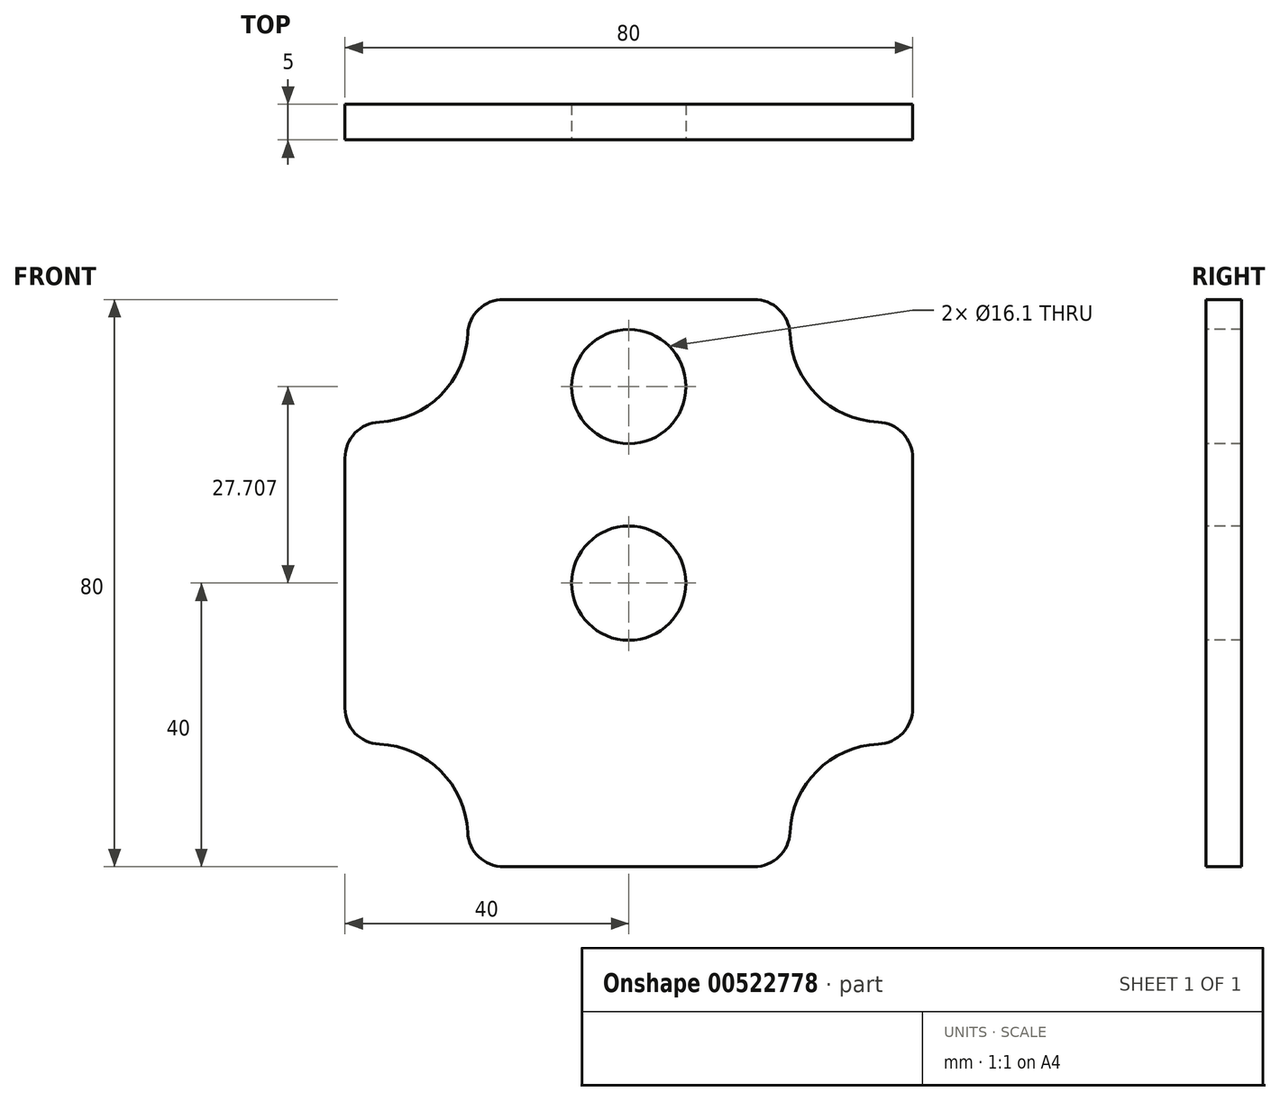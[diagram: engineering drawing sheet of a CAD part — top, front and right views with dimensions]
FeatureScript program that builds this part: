
annotation { "Feature Type Name" : "Feature", "Feature Type Description" : "" }
export const myFeature = defineFeature(function(context is Context, id is Id, definition is map)
    precondition{}
    {
        {
            var Q0;
            Q0=qCreatedBy(makeId("Front.planeOp"),FACE);
            var sketch = newSketch(context, id + "F0", { "sketchPlane" : qUnion([Q0])});
            skLineSegment(sketch, "E0", {"start": v(-40, 0) * mm, "end": v(-40, 23.43) * mm});
            skLineSegment(sketch, "E1", {"start": v(-40, 23.43) * mm, "end": v(-23.43, 40) * mm});
            skLineSegment(sketch, "E2", {"start": v(-23.43, 40) * mm, "end": v(0, 40) * mm});
            skLineSegment(sketch, "E3", {"start": v(-40, 0) * mm, "end": v(0, 0) * mm});
            skLineSegment(sketch, "E4", {"start": v(0, 0) * mm, "end": v(0, 40) * mm});
            skArc(sketch, "E5", {"start": v(-40, 23.43) * mm, "mid": v(-26.5, 26.5) * mm, "end": v(-23.43, 40) * mm});
            skSolve(sketch);
        }
        {
            var Q0;
            Q0=makeQuery(id+"F0.imprint","IMPRINT",FACE,{"disambiguationData":[TD([[makeQuery(id+"F0.imprint","IMPRINT",EDGE,{"derivedFrom":sQuery(id+"F0.wireOp",EDGE,"E0")}),-1.0]])]});
            extrude(context, id + "F1", {"entities" : qUnion([Q0]), "depth" : 5 * mm, "offsetDistance" : 25.4 * mm});
        }
        {
            var Q0;
            Q0=makeQuery(id+"F1.opExtrude","SWEPT_BODY",BODY,{"disambiguationData":[OSD([sQuery(id+"F0.wireOp",EDGE,"E0"),sQuery(id+"F0.wireOp",EDGE,"E1"),sQuery(id+"F0.wireOp",EDGE,"E2"),sQuery(id+"F0.wireOp",EDGE,"E3"),sQuery(id+"F0.wireOp",EDGE,"E4")])]});
            var Q1;
            Q1=makeQuery(id+"F1.opExtrude","SWEPT_FACE",FACE,{"disambiguationData":[OSD([sQuery(id+"F0.wireOp",EDGE,"E4")])]});
            mirror(context, id + "F2", {"operationType" : NewBodyOperationType.ADD, "entities" : qUnion([Q0]), "mirrorPlane" : qUnion([Q1])});
        }
        {
            var Q0;
            Q0=makeQuery(id+"F1.opExtrude","SWEPT_BODY",BODY,{"disambiguationData":[OSD([sQuery(id+"F0.wireOp",EDGE,"E0"),sQuery(id+"F0.wireOp",EDGE,"E1"),sQuery(id+"F0.wireOp",EDGE,"E2"),sQuery(id+"F0.wireOp",EDGE,"E3"),sQuery(id+"F0.wireOp",EDGE,"E4")])]});
            var Q1;
            {var subQ0=makeQuery(id+"F1.opExtrude","SWEPT_FACE",FACE,{"disambiguationData":[OSD([sQuery(id+"F0.wireOp",EDGE,"E3")])]});Q1=makeQuery(id+"F2.boolean.opBoolean","MERGE",FACE,{"derivedFrom":[subQ0,makeQuery(id+"F2.opPattern","COPY",FACE,{"derivedFrom":subQ0,"instanceName":"1"})]});}
            mirror(context, id + "F3", {"operationType" : NewBodyOperationType.ADD, "entities" : qUnion([Q0]), "mirrorPlane" : qUnion([Q1])});
        }
        {
            var Q0;
            {var subQ0=makeQuery(id+"F1.opExtrude","CAP_FACE",FACE,{"disambiguationData":[OSD([sQuery(id+"F0.wireOp",EDGE,"E0"),sQuery(id+"F0.wireOp",EDGE,"E1"),sQuery(id+"F0.wireOp",EDGE,"E2"),sQuery(id+"F0.wireOp",EDGE,"E3"),sQuery(id+"F0.wireOp",EDGE,"E4")])],"isStart":false});var subQ1=makeQuery(id+"F2.boolean.opBoolean","MERGE",FACE,{"derivedFrom":[subQ0,makeQuery(id+"F2.opPattern","COPY",FACE,{"derivedFrom":subQ0,"instanceName":"1"})]});Q0=makeQuery(id+"F3.boolean.opBoolean","MERGE",FACE,{"derivedFrom":[subQ1,makeQuery(id+"F3.opPattern","COPY",FACE,{"derivedFrom":subQ1,"instanceName":"1"})]});}
            var sketch = newSketch(context, id + "F4", { "sketchPlane" : qUnion([Q0])});
            skCircle(sketch, "E6", {"center": v(0, 0) * mm, "radius": 8.05 * mm});
            skCircle(sketch, "E7.0", {"center": v(0, 0) * mm, "radius": 14.4 * mm});
            skSolve(sketch);
        }
        {
            var Q0;
            Q0=makeQuery(id+"F4.imprint","IMPRINT",FACE,{"disambiguationData":[TD([[makeQuery(id+"F4.imprint","IMPRINT",EDGE,{"derivedFrom":sQuery(id+"F4.wireOp",EDGE,"E6")}),1.0]])]});
            extrude(context, id + "F5", {"entities" : qUnion([Q0]), "operationType" : NewBodyOperationType.REMOVE, "endBound" : BoundingType.THROUGH_ALL, "oppositeDirection" : true, "depth" : 25.4 * mm, "offsetDistance" : 25.4 * mm});
        }
        {
            var Q0;
            Q0=makeQuery(id+"F1.opExtrude","SWEPT_EDGE",EDGE,{"disambiguationData":[OSD([sQuery(id+"F0.wireOp",EDGE,"E0"),sQuery(id+"F0.wireOp",EDGE,"E1"),sQuery(id+"F0.wireOp",EDGE,"E5")])]});
            var Q1;
            Q1=makeQuery(id+"F1.opExtrude","SWEPT_EDGE",EDGE,{"disambiguationData":[OSD([sQuery(id+"F0.wireOp",EDGE,"E1"),sQuery(id+"F0.wireOp",EDGE,"E2"),sQuery(id+"F0.wireOp",EDGE,"E5")])]});
            var Q2;
            Q2=makeQuery(id+"F2.opPattern","COPY",EDGE,{"derivedFrom":makeQuery(id+"F1.opExtrude","SWEPT_EDGE",EDGE,{"disambiguationData":[OSD([sQuery(id+"F0.wireOp",EDGE,"E1"),sQuery(id+"F0.wireOp",EDGE,"E2"),sQuery(id+"F0.wireOp",EDGE,"E5")])]}),"instanceName":"1"});
            var Q3;
            Q3=makeQuery(id+"F2.opPattern","COPY",EDGE,{"derivedFrom":makeQuery(id+"F1.opExtrude","SWEPT_EDGE",EDGE,{"disambiguationData":[OSD([sQuery(id+"F0.wireOp",EDGE,"E0"),sQuery(id+"F0.wireOp",EDGE,"E1"),sQuery(id+"F0.wireOp",EDGE,"E5")])]}),"instanceName":"1"});
            var Q4;
            Q4=makeQuery(id+"F3.opPattern","COPY",EDGE,{"derivedFrom":makeQuery(id+"F2.opPattern","COPY",EDGE,{"derivedFrom":makeQuery(id+"F1.opExtrude","SWEPT_EDGE",EDGE,{"disambiguationData":[OSD([sQuery(id+"F0.wireOp",EDGE,"E0"),sQuery(id+"F0.wireOp",EDGE,"E1"),sQuery(id+"F0.wireOp",EDGE,"E5")])]}),"instanceName":"1"}),"instanceName":"1"});
            var Q5;
            Q5=makeQuery(id+"F3.opPattern","COPY",EDGE,{"derivedFrom":makeQuery(id+"F2.opPattern","COPY",EDGE,{"derivedFrom":makeQuery(id+"F1.opExtrude","SWEPT_EDGE",EDGE,{"disambiguationData":[OSD([sQuery(id+"F0.wireOp",EDGE,"E1"),sQuery(id+"F0.wireOp",EDGE,"E2"),sQuery(id+"F0.wireOp",EDGE,"E5")])]}),"instanceName":"1"}),"instanceName":"1"});
            var Q6;
            Q6=makeQuery(id+"F3.opPattern","COPY",EDGE,{"derivedFrom":makeQuery(id+"F1.opExtrude","SWEPT_EDGE",EDGE,{"disambiguationData":[OSD([sQuery(id+"F0.wireOp",EDGE,"E0"),sQuery(id+"F0.wireOp",EDGE,"E1"),sQuery(id+"F0.wireOp",EDGE,"E5")])]}),"instanceName":"1"});
            var Q7;
            Q7=makeQuery(id+"F3.opPattern","COPY",EDGE,{"derivedFrom":makeQuery(id+"F1.opExtrude","SWEPT_EDGE",EDGE,{"disambiguationData":[OSD([sQuery(id+"F0.wireOp",EDGE,"E1"),sQuery(id+"F0.wireOp",EDGE,"E2"),sQuery(id+"F0.wireOp",EDGE,"E5")])]}),"instanceName":"1"});
            fillet(context, id + "F6", {"entities" : qUnion([Q0, Q1, Q2, Q3, Q4, Q5, Q6, Q7]), "radius" : 5.08 * mm, "tangentPropagation" : true, "allowEdgeOverflow" : false});
        }
        {
            var Q0;
            Q0=makeQuery(id+"F4.imprint","IMPRINT",FACE,{"disambiguationData":[TD([[makeQuery(id+"F4.imprint","IMPRINT",EDGE,{"derivedFrom":sQuery(id+"F4.wireOp",EDGE,"E7.0")}),-1.0]])]});
            var sketch = newSketch(context, id + "F7", { "sketchPlane" : qUnion([Q0])});
            skCircle(sketch, "E8", {"center": v(0, 27.7) * mm, "radius": 8.05 * mm});
            skSolve(sketch);
        }
        {
            var Q0;
            Q0 = qSketchRegion(id + "F7", true);
            extrude(context, id + "F8", {"entities" : qUnion([Q0]), "operationType" : NewBodyOperationType.REMOVE, "endBound" : BoundingType.THROUGH_ALL, "oppositeDirection" : true, "depth" : 25 * mm, "offsetDistance" : 25 * mm});
        }
    });
